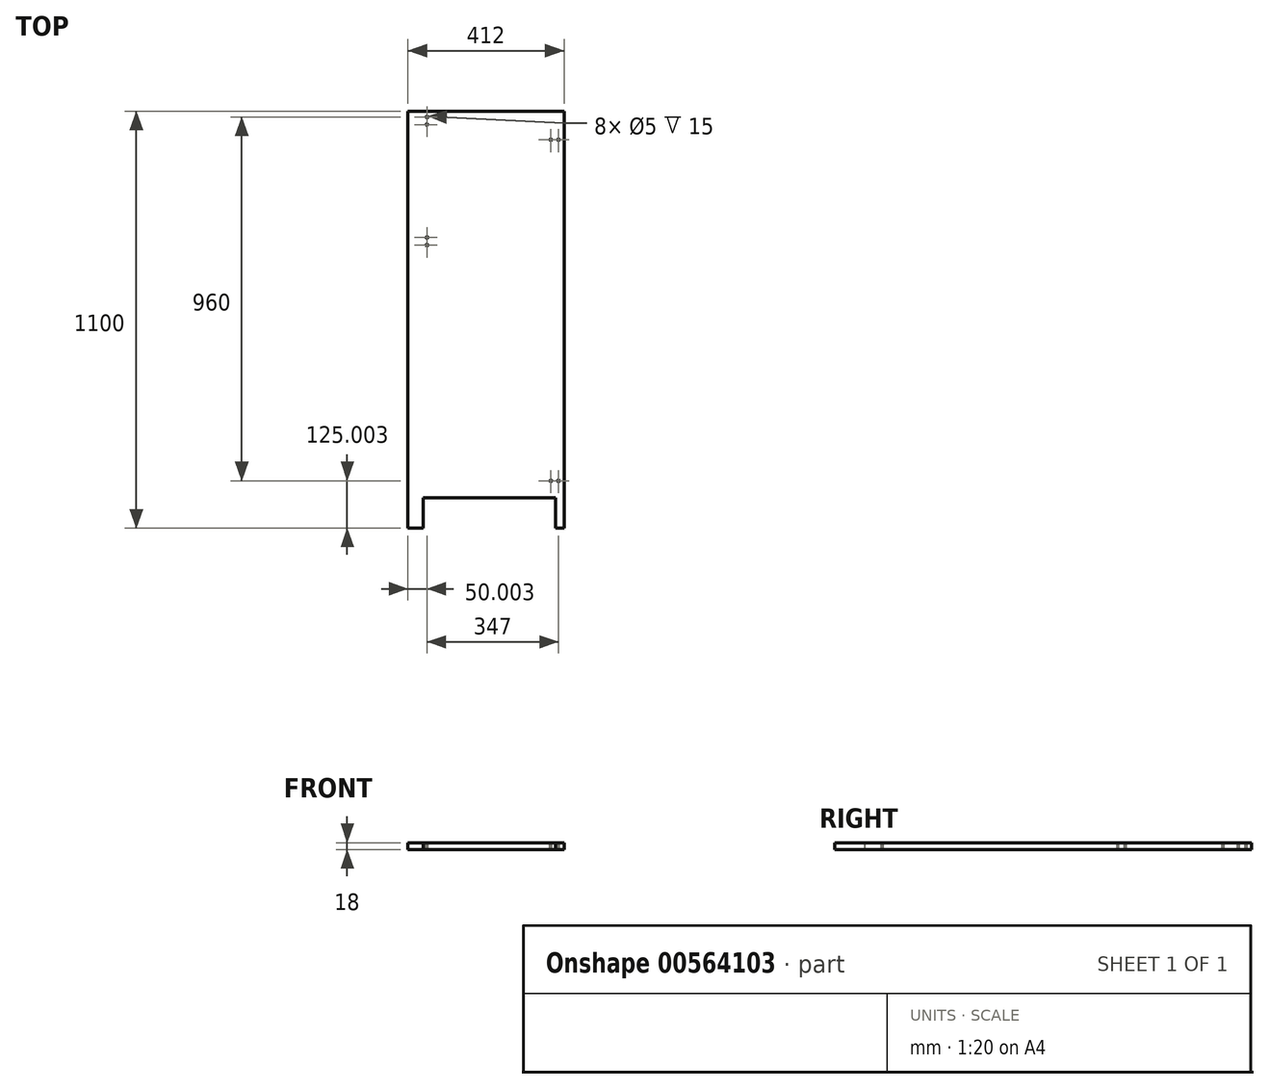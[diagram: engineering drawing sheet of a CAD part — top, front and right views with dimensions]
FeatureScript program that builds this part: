
annotation { "Feature Type Name" : "Feature", "Feature Type Description" : "" }
export const myFeature = defineFeature(function(context is Context, id is Id, definition is map)
    precondition{}
    {
        {
            var Q0;
            Q0=qCreatedBy(makeId("Top.planeOp"),FACE);
            var sketch = newSketch(context, id + "F0", { "sketchPlane" : qUnion([Q0])});
            skLineSegment(sketch, "E0.bottom", {"start": v(-202.45, 853.48) * mm, "end": v(209.55, 853.48) * mm});
            skLineSegment(sketch, "E0.top", {"start": v(-202.45, -246.52) * mm, "end": v(209.55, -246.52) * mm});
            skLineSegment(sketch, "E0.left", {"start": v(-202.45, 853.48) * mm, "end": v(-202.45, -246.52) * mm});
            skLineSegment(sketch, "E0.right", {"start": v(209.55, 853.48) * mm, "end": v(209.55, -246.52) * mm});
            skSolve(sketch);
        }
        {
            var Q0;
            Q0=makeQuery(id+"F0.imprint","IMPRINT",FACE,{"disambiguationData":[TD([[makeQuery(id+"F0.imprint","IMPRINT",EDGE,{"derivedFrom":sQuery(id+"F0.wireOp",EDGE,"E0.bottom")}),-1.0]])]});
            extrude(context, id + "F1", {"entities" : qUnion([Q0]), "depth" : 18 * mm, "offsetDistance" : 25 * mm});
        }
        {
            var Q0;
            Q0=makeQuery(id+"F1.opExtrude","CAP_FACE",FACE,{"disambiguationData":[OSD([sQuery(id+"F0.wireOp",EDGE,"E0.bottom"),sQuery(id+"F0.wireOp",EDGE,"E0.top"),sQuery(id+"F0.wireOp",EDGE,"E0.left"),sQuery(id+"F0.wireOp",EDGE,"E0.right")])],"isStart":false});
            var sketch = newSketch(context, id + "F2", { "sketchPlane" : qUnion([Q0])});
            skLineSegment(sketch, "E1.bottom", {"start": v(209.55, -246.52) * mm, "end": v(-162.45, -246.52) * mm});
            skLineSegment(sketch, "E1.top", {"start": v(187.55, -166.52) * mm, "end": v(-162.45, -166.52) * mm});
            skLineSegment(sketch, "E1.left", {"start": v(187.55, -246.52) * mm, "end": v(187.55, -166.52) * mm});
            skLineSegment(sketch, "E1.right", {"start": v(-162.45, -246.52) * mm, "end": v(-162.45, -166.52) * mm});
            skSolve(sketch);
        }
        {
            var Q0;
            Q0=makeQuery(id+"F2.imprint","IMPRINT",FACE,{"disambiguationData":[TD([[makeQuery(id+"F2.imprint","IMPRINT",EDGE,{"derivedFrom":sQuery(id+"F2.wireOp",EDGE,"E1.bottom")}),1.0]])]});
            extrude(context, id + "F3", {"entities" : qUnion([Q0]), "operationType" : NewBodyOperationType.REMOVE, "oppositeDirection" : true, "depth" : 25 * mm, "offsetDistance" : 25 * mm});
        }
        {
            var Q0;
            Q0=makeQuery(id+"F1.opExtrude","CAP_FACE",FACE,{"disambiguationData":[OSD([sQuery(id+"F0.wireOp",EDGE,"E0.bottom"),sQuery(id+"F0.wireOp",EDGE,"E0.top"),sQuery(id+"F0.wireOp",EDGE,"E0.left"),sQuery(id+"F0.wireOp",EDGE,"E0.right")])],"isStart":false});
            var sketch = newSketch(context, id + "F4", { "sketchPlane" : qUnion([Q0])});
            skCircle(sketch, "E2", {"center": v(194.55, 778.48) * mm, "radius": 2.5 * mm});
            skCircle(sketch, "E3", {"center": v(174.55, 778.48) * mm, "radius": 2.5 * mm});
            skCircle(sketch, "E4", {"center": v(-152.45, 818.48) * mm, "radius": 2.5 * mm});
            skCircle(sketch, "E5", {"center": v(-152.45, 838.48) * mm, "radius": 2.5 * mm});
            skCircle(sketch, "E6", {"center": v(194.55, -121.52) * mm, "radius": 2.5 * mm});
            skCircle(sketch, "E7", {"center": v(174.55, -121.52) * mm, "radius": 2.5 * mm});
            skCircle(sketch, "E8", {"center": v(-152.45, 520.48) * mm, "radius": 2.5 * mm});
            skCircle(sketch, "E9", {"center": v(-152.45, 500.48) * mm, "radius": 2.5 * mm});
            skSolve(sketch);
        }
        {
            var Q0;
            Q0 = qSketchRegion(id + "F4", true);
            extrude(context, id + "F5", {"entities" : qUnion([Q0]), "operationType" : NewBodyOperationType.REMOVE, "oppositeDirection" : true, "depth" : 15 * mm, "offsetDistance" : 25 * mm});
        }
    });
